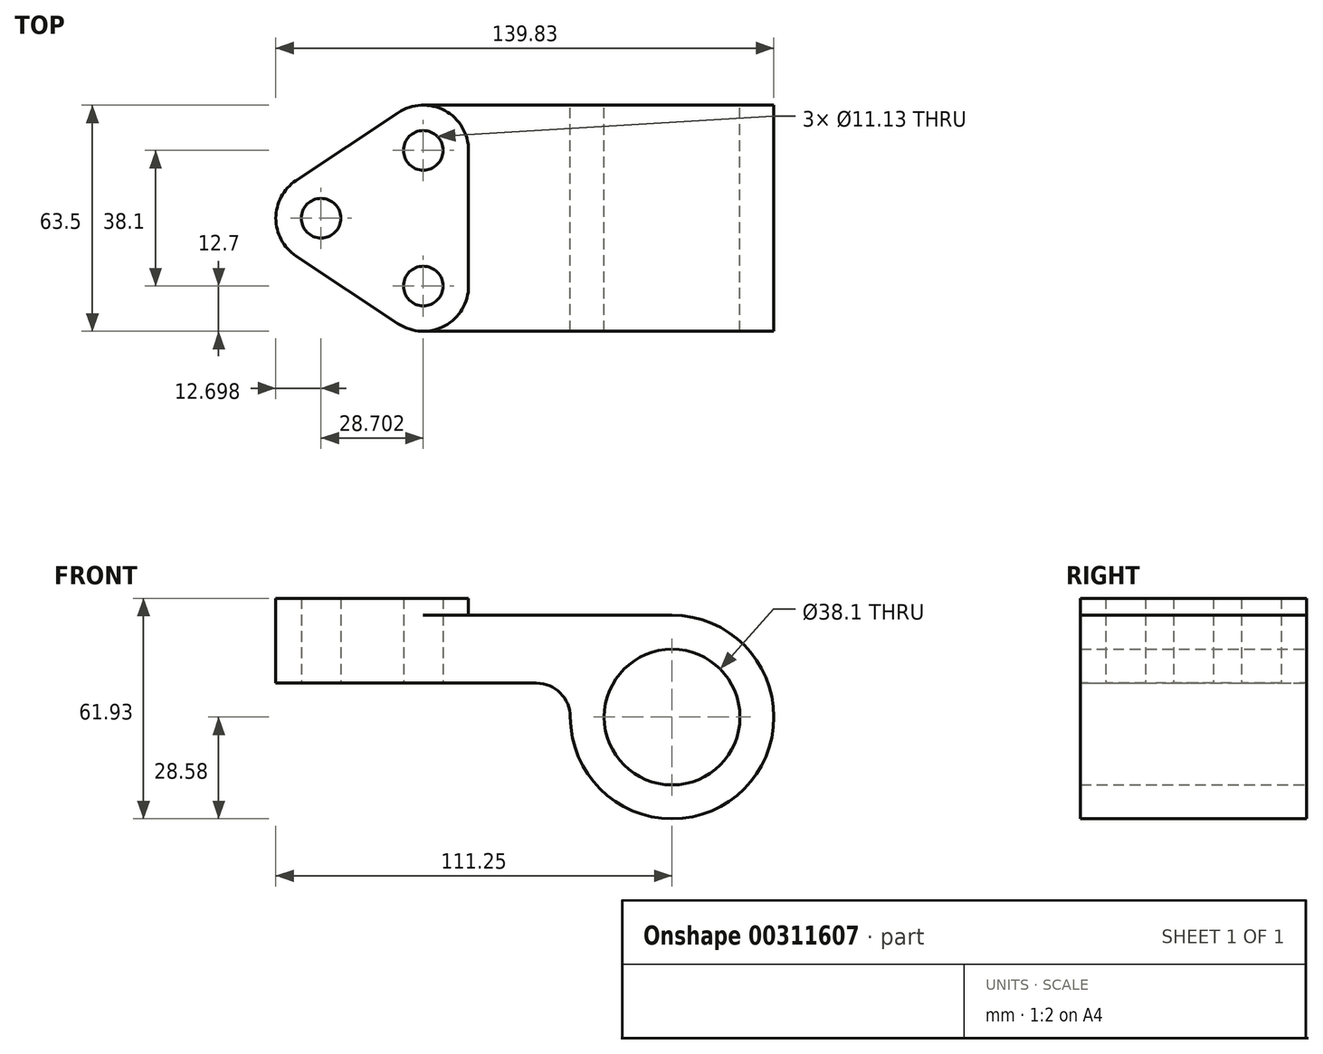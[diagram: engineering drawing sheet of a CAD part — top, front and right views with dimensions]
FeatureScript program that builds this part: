
annotation { "Feature Type Name" : "Feature", "Feature Type Description" : "" }
export const myFeature = defineFeature(function(context is Context, id is Id, definition is map)
    precondition{}
    {
        {
            var Q0;
            Q0=qCreatedBy(makeId("Front.planeOp"),FACE);
            var sketch = newSketch(context, id + "F0", { "sketchPlane" : qUnion([Q0])});
            skCircle(sketch, "E0", {"center": v(0, 0) * mm, "radius": 19.05 * mm});
            skLineSegment(sketch, "E1", {"start": v(0, 28.58) * mm, "end": v(-69.85, 28.57) * mm});
            skLineSegment(sketch, "E2", {"start": v(-69.85, 28.57) * mm, "end": v(-69.85, 9.52) * mm});
            skLineSegment(sketch, "E3", {"start": v(-69.85, 9.52) * mm, "end": v(-38.1, 9.52) * mm});
            skArc(sketch, "E4", {"start": v(-28.58, 0) * mm, "mid": v(-31.36, 6.74) * mm, "end": v(-38.1, 9.52) * mm});
            skArc(sketch, "E5", {"start": v(-28.58, 0) * mm, "mid": v(20.2, -20.2) * mm, "end": v(0, 28.58) * mm});
            skSolve(sketch);
        }
        {
            var Q0;
            Q0 = qSketchRegion(id + "F0", true);
            extrude(context, id + "F1", {"entities" : qUnion([Q0]), "depth" : 63.5 * mm});
        }
        {
            var Q0;
            Q0=makeQuery(id+"F1.opExtrude","SWEPT_FACE",FACE,{"disambiguationData":[OSD([sQuery(id+"F0.wireOp",EDGE,"E1")])]});
            var sketch = newSketch(context, id + "F2", { "sketchPlane" : qUnion([Q0])});
            skLineSegment(sketch, "E6", {"start": v(-69.85, -50.8) * mm, "end": v(-69.85, -12.7) * mm, "construction": true});
            skLineSegment(sketch, "E7", {"start": v(-69.85, -12.7) * mm, "end": v(-98.55, -31.75) * mm, "construction": true});
            skLineSegment(sketch, "E8", {"start": v(-98.55, -31.75) * mm, "end": v(-69.85, -50.8) * mm, "construction": true});
            skArc(sketch, "E9", {"start": v(-105.58, -21.17) * mm, "mid": v(-111.25, -31.75) * mm, "end": v(-105.58, -42.33) * mm});
            skLineSegment(sketch, "E10", {"start": v(-105.58, -42.33) * mm, "end": v(-76.87, -61.38) * mm});
            skArc(sketch, "E11", {"start": v(-76.87, -61.38) * mm, "mid": v(-63.85, -62) * mm, "end": v(-57.15, -50.8) * mm});
            skLineSegment(sketch, "E12", {"start": v(-57.15, -50.8) * mm, "end": v(-57.15, -12.7) * mm});
            skArc(sketch, "E13", {"start": v(-57.15, -12.7) * mm, "mid": v(-63.85, -1.5) * mm, "end": v(-76.87, -2.12) * mm});
            skLineSegment(sketch, "E14", {"start": v(-76.87, -2.12) * mm, "end": v(-105.58, -21.17) * mm});
            skCircle(sketch, "E15", {"center": v(-98.55, -31.75) * mm, "radius": 5.56 * mm});
            skCircle(sketch, "E16", {"center": v(-69.85, -50.8) * mm, "radius": 5.56 * mm});
            skCircle(sketch, "E17", {"center": v(-69.85, -12.7) * mm, "radius": 5.56 * mm});
            skSolve(sketch);
        }
        {
            var Q0;
            Q0 = qSketchRegion(id + "F2", true);
            var Q1;
            {var subQ0=sQuery(id+"F2.wireOp",EDGE,"E16");var subQ1=makeQuery(id+"F1.opExtrude","SWEPT_EDGE",EDGE,{"disambiguationData":[OSD([sQuery(id+"F0.wireOp",EDGE,"E1"),sQuery(id+"F0.wireOp",EDGE,"E2")])]});var subQ2=makeQuery(id+"F2.imprint","INTERSECT",VERTEX,{"disambiguationData":[OD(0.0)],"derivedFrom":[subQ1,subQ0]});Q1=makeQuery(id+"F2.imprint","IMPRINT",FACE,{"disambiguationData":[TD([[makeQuery(id+"F2.imprint","IMPRINT",EDGE,{"disambiguationData":[TD([[subQ2,-1.0]])],"derivedFrom":subQ0}),1.0]])]});}
            var Q2;
            Q2=makeQuery(id+"F1.opExtrude","SWEPT_FACE",FACE,{"disambiguationData":[OSD([sQuery(id+"F0.wireOp",EDGE,"E3")])]});
            extrude(context, id + "F3", {"entities" : qUnion([Q0, Q1]), "operationType" : NewBodyOperationType.ADD, "endBoundEntityFace" : qUnion([Q2]), "depth" : 4.78 * mm});
        }
        {
            var Q0;
            {var subQ0=sQuery(id+"F2.wireOp",EDGE,"E16");var subQ1=makeQuery(id+"F1.opExtrude","SWEPT_EDGE",EDGE,{"disambiguationData":[OSD([sQuery(id+"F0.wireOp",EDGE,"E1"),sQuery(id+"F0.wireOp",EDGE,"E2")])]});var subQ2=makeQuery(id+"F2.imprint","INTERSECT",VERTEX,{"disambiguationData":[OD(0.0)],"derivedFrom":[subQ1,subQ0]});Q0=makeQuery(id+"F2.imprint","IMPRINT",FACE,{"disambiguationData":[TD([[makeQuery(id+"F2.imprint","IMPRINT",EDGE,{"disambiguationData":[TD([[subQ2,-1.0]])],"derivedFrom":subQ0}),1.0]])]});}
            var Q1;
            {var subQ0=sQuery(id+"F2.wireOp",EDGE,"E17");var subQ1=makeQuery(id+"F1.opExtrude","SWEPT_EDGE",EDGE,{"disambiguationData":[OSD([sQuery(id+"F0.wireOp",EDGE,"E1"),sQuery(id+"F0.wireOp",EDGE,"E2")])]});var subQ2=makeQuery(id+"F2.imprint","INTERSECT",VERTEX,{"disambiguationData":[OD(0.0)],"derivedFrom":[subQ1,subQ0]});Q1=makeQuery(id+"F2.imprint","IMPRINT",FACE,{"disambiguationData":[TD([[makeQuery(id+"F2.imprint","IMPRINT",EDGE,{"disambiguationData":[TD([[subQ2,1.0]])],"derivedFrom":subQ0}),1.0]])]});}
            extrude(context, id + "F4", {"entities" : qUnion([Q0, Q1]), "operationType" : NewBodyOperationType.REMOVE, "endBound" : BoundingType.THROUGH_ALL, "oppositeDirection" : true, "depth" : 25.4 * mm, "hasSecondDirection" : true, "secondDirectionBound" : SecondDirectionBoundingType.THROUGH_ALL, "secondDirectionOppositeDirection" : false, "secondDirectionDepth" : 25.4 * mm});
        }
        {
            var Q0;
            Q0=makeQuery(id+"F2.imprint","IMPRINT",FACE,{"disambiguationData":[TD([[makeQuery(id+"F2.imprint","IMPRINT",EDGE,{"derivedFrom":sQuery(id+"F2.wireOp",EDGE,"E9")}),1.0]])]});
            var Q1;
            {var subQ7=sQuery(id+"F2.wireOp",EDGE,"E12");Q1=makeQuery(id+"F2.imprint","IMPRINT",FACE,{"disambiguationData":[TD([[makeQuery(id+"F2.imprint","IMPRINT",EDGE,{"derivedFrom":subQ7}),1.0]])]});}
            var Q2;
            Q2=makeQuery(id+"F1.opExtrude","SWEPT_FACE",FACE,{"disambiguationData":[OSD([sQuery(id+"F0.wireOp",EDGE,"E3")])]});
            extrude(context, id + "F5", {"entities" : qUnion([Q0, Q1]), "operationType" : NewBodyOperationType.ADD, "endBound" : BoundingType.UP_TO_SURFACE, "oppositeDirection" : true, "endBoundEntityFace" : qUnion([Q2]), "depth" : 25.4 * mm});
        }
    });
